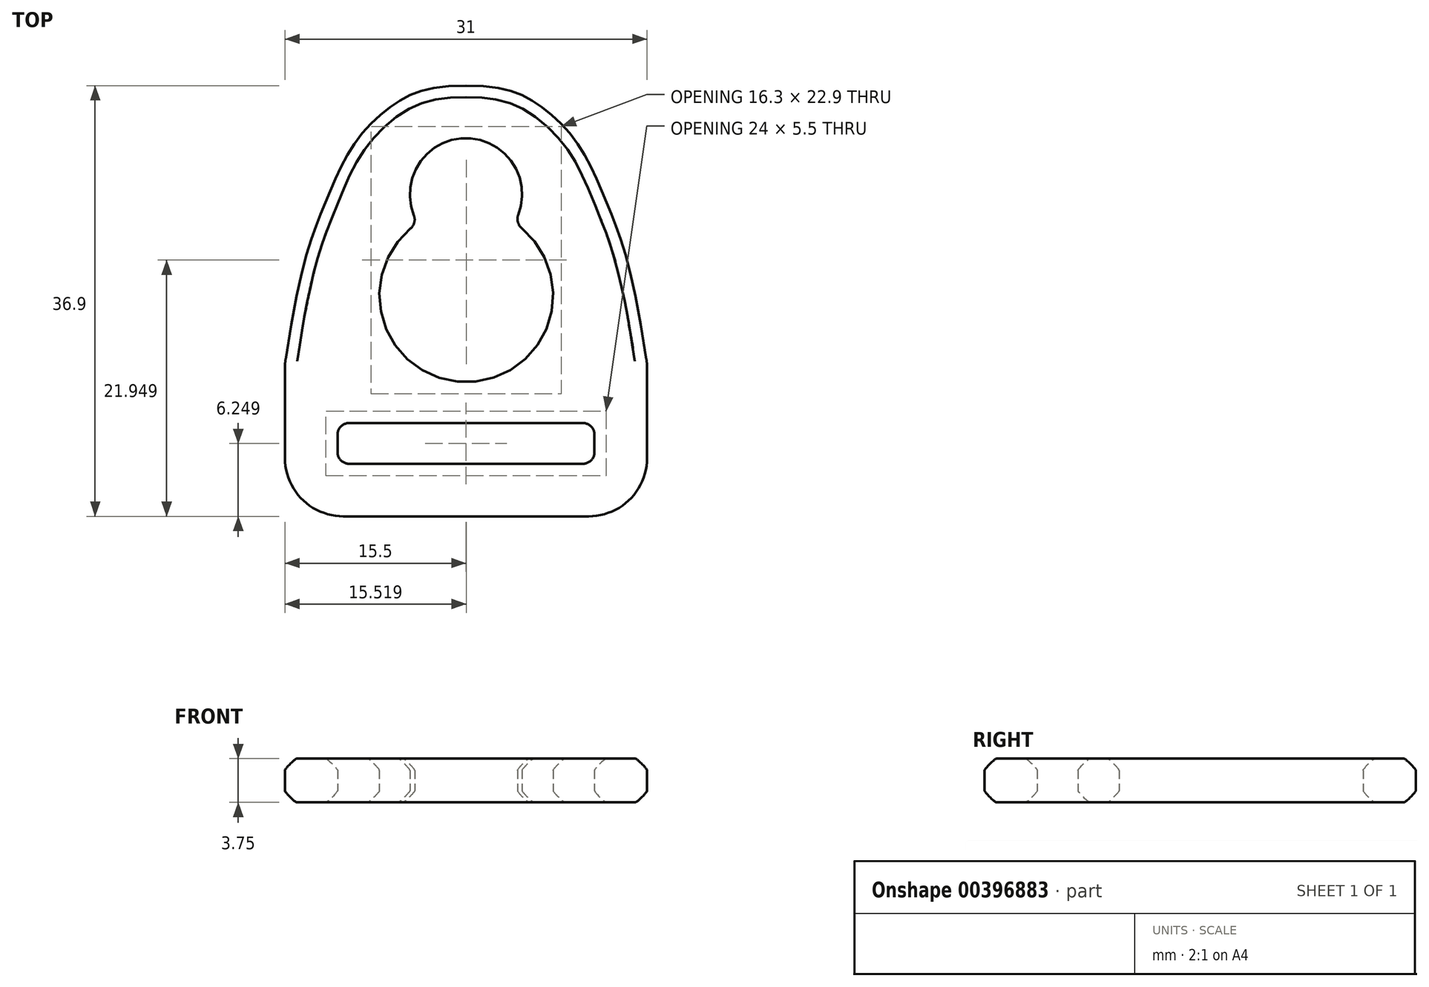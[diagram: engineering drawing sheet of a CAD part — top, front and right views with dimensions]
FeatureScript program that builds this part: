
annotation { "Feature Type Name" : "Feature", "Feature Type Description" : "" }
export const myFeature = defineFeature(function(context is Context, id is Id, definition is map)
    precondition{}
    {
        {
            var Q0;
            Q0=qCreatedBy(makeId("Top.planeOp"),FACE);
            var sketch = newSketch(context, id + "F0", { "sketchPlane" : qUnion([Q0])});
            skCircle(sketch, "E0", {"center": v(0.03, 5.86) * mm, "radius": 7.45 * mm});
            skCircle(sketch, "E1", {"center": v(0, 14.5) * mm, "radius": 4.8 * mm});
            skLineSegment(sketch, "E2", {"start": v(0, -1.58) * mm, "end": v(0, 19.32) * mm, "construction": true});
            skLineSegment(sketch, "E3.bottom", {"start": v(11, -8.58) * mm, "end": v(-11, -8.58) * mm});
            skLineSegment(sketch, "E3.top", {"start": v(11, -5.08) * mm, "end": v(-11, -5.08) * mm});
            skLineSegment(sketch, "E3.left", {"start": v(11, -8.58) * mm, "end": v(11, -5.08) * mm});
            skLineSegment(sketch, "E3.right", {"start": v(-11, -8.58) * mm, "end": v(-11, -5.08) * mm});
            skPoint(sketch, "E3.middle", {"position": v(0, -6.83) * mm});
            skLineSegment(sketch, "E4", {"start": v(0, -1.58) * mm, "end": v(0, -5.08) * mm, "construction": true});
            skPoint(sketch, "E4.endSnap0", {"position": v(0, -5.08) * mm});
            skLineSegment(sketch, "E5", {"start": v(-11, -8.58) * mm, "end": v(-15.5, -8.58) * mm, "construction": true});
            skLineSegment(sketch, "E6", {"start": v(-15.5, -8.58) * mm, "end": v(-15.5, -13.08) * mm, "construction": true});
            skLineSegment(sketch, "E7", {"start": v(11, -6.83) * mm, "end": v(15.5, -6.83) * mm, "construction": true});
            skLineSegment(sketch, "E8", {"start": v(0, 19.32) * mm, "end": v(0, 23.82) * mm, "construction": true});
            skLineSegment(sketch, "E9.bottom", {"start": v(-15.5, -13.08) * mm, "end": v(15.5, -13.08) * mm});
            skLineSegment(sketch, "E9.top", {"start": v(-15.5, 23.82) * mm, "end": v(15.5, 23.82) * mm});
            skLineSegment(sketch, "E9.left", {"start": v(-15.5, -13.08) * mm, "end": v(-15.5, 23.82) * mm});
            skLineSegment(sketch, "E9.right", {"start": v(15.5, -13.08) * mm, "end": v(15.5, 23.82) * mm});
            skFitSpline(sketch, "E10", {"points": [v(-15.5, 0) * mm, v(-12.1, 13.64) * mm, v(-9.63, 18.74) * mm, v(-5.82, 22.43) * mm, v(0, 23.82) * mm], "startDerivative": vector(11.5, 77.14) * mm, "endDerivative": vector(37.83, 0) * mm});
            skFitSpline(sketch, "E11.MirrorCS", {"points": [v(15.5, 0) * mm, v(12.1, 13.64) * mm, v(9.63, 18.74) * mm, v(5.82, 22.43) * mm, v(0, 23.82) * mm], "startDerivative": vector(-11.5, 77.14) * mm, "endDerivative": vector(-37.83, 0) * mm});
            skLineSegment(sketch, "E12", {"start": v(-4.13, 12.04) * mm, "end": v(4.13, 12.04) * mm, "construction": true});
            skSolve(sketch);
        }
        {
            var Q0;
            Q0=makeQuery(id+"F0.imprint","IMPRINT",FACE,{"disambiguationData":[TD([[makeQuery(id+"F0.imprint","IMPRINT",EDGE,{"derivedFrom":sQuery(id+"F0.wireOp",EDGE,"E3.bottom")}),1.0]])]});
            extrude(context, id + "F1", {"entities" : qUnion([Q0]), "depth" : 3.75 * mm});
        }
        {
            var Q0;
            Q0=makeQuery(id+"F1.opExtrude","SWEPT_EDGE",EDGE,{"disambiguationData":[OSD([sQuery(id+"F0.wireOp",EDGE,"E9.left"),sQuery(id+"F0.wireOp",EDGE,"E10")])]});
            var Q1;
            Q1=makeQuery(id+"F1.opExtrude","SWEPT_EDGE",EDGE,{"disambiguationData":[OSD([sQuery(id+"F0.wireOp",EDGE,"E9.bottom"),sQuery(id+"F0.wireOp",EDGE,"E9.left")])]});
            var Q2;
            Q2=makeQuery(id+"F1.opExtrude","SWEPT_EDGE",EDGE,{"disambiguationData":[OSD([sQuery(id+"F0.wireOp",EDGE,"E9.right"),sQuery(id+"F0.wireOp",EDGE,"E11.MirrorCS")])]});
            var Q3;
            Q3=makeQuery(id+"F1.opExtrude","SWEPT_EDGE",EDGE,{"disambiguationData":[OSD([sQuery(id+"F0.wireOp",EDGE,"E9.bottom"),sQuery(id+"F0.wireOp",EDGE,"E9.right")])]});
            fillet(context, id + "F2", {"entities" : qUnion([Q0, Q1, Q2, Q3]), "radius" : 5 * mm, "tangentPropagation" : true, "allowEdgeOverflow" : false});
        }
        {
            var Q0;
            Q0=makeQuery(id+"F1.opExtrude","SWEPT_EDGE",EDGE,{"disambiguationData":[OSD([sQuery(id+"F0.wireOp",EDGE,"E3.top"),sQuery(id+"F0.wireOp",EDGE,"E3.right")])]});
            var Q1;
            Q1=makeQuery(id+"F1.opExtrude","SWEPT_EDGE",EDGE,{"disambiguationData":[OSD([sQuery(id+"F0.wireOp",EDGE,"E3.bottom"),sQuery(id+"F0.wireOp",EDGE,"E3.right")])]});
            var Q2;
            Q2=makeQuery(id+"F1.opExtrude","SWEPT_EDGE",EDGE,{"disambiguationData":[OSD([sQuery(id+"F0.wireOp",EDGE,"E3.top"),sQuery(id+"F0.wireOp",EDGE,"E3.left")])]});
            var Q3;
            Q3=makeQuery(id+"F1.opExtrude","SWEPT_EDGE",EDGE,{"disambiguationData":[OSD([sQuery(id+"F0.wireOp",EDGE,"E3.bottom"),sQuery(id+"F0.wireOp",EDGE,"E3.left")])]});
            var Q4;
            {var subQ0=sQuery(id+"F0.wireOp",EDGE,"E1");var subQ1=sQuery(id+"F0.wireOp",EDGE,"E0");Q4=makeQuery(id+"F1.opExtrude","SWEPT_EDGE",EDGE,{"disambiguationData":[OSD([subQ1,subQ0]),TDD([makeQuery(id+"F0.imprint","INTERSECT",VERTEX,{"disambiguationData":[OD(0.0)],"derivedFrom":[subQ1,subQ0]})])]});}
            var Q5;
            {var subQ0=sQuery(id+"F0.wireOp",EDGE,"E1");var subQ1=sQuery(id+"F0.wireOp",EDGE,"E0");Q5=makeQuery(id+"F1.opExtrude","SWEPT_EDGE",EDGE,{"disambiguationData":[OSD([subQ1,subQ0]),TDD([makeQuery(id+"F0.imprint","INTERSECT",VERTEX,{"disambiguationData":[OD(1.0)],"derivedFrom":[subQ1,subQ0]})])]});}
            fillet(context, id + "F3", {"entities" : qUnion([Q0, Q1, Q2, Q3, Q4, Q5]), "radius" : 1 * mm, "tangentPropagation" : true, "allowEdgeOverflow" : false});
        }
        {
            var Q0;
            Q0=makeQuery(id+"F1.opExtrude","CAP_EDGE",EDGE,{"disambiguationData":[OSD([sQuery(id+"F0.wireOp",EDGE,"E3.top")])],"isStart":false});
            var Q1;
            Q1=makeQuery(id+"F1.opExtrude","CAP_EDGE",EDGE,{"disambiguationData":[OSD([sQuery(id+"F0.wireOp",EDGE,"E3.top")])],"isStart":true});
            var Q2;
            Q2=makeQuery(id+"F1.opExtrude","CAP_EDGE",EDGE,{"disambiguationData":[OSD([sQuery(id+"F0.wireOp",EDGE,"E0")])],"isStart":false});
            var Q3;
            Q3=makeQuery(id+"F1.opExtrude","CAP_EDGE",EDGE,{"disambiguationData":[OSD([sQuery(id+"F0.wireOp",EDGE,"E0")])],"isStart":true});
            var Q4;
            Q4=makeQuery(id+"F1.opExtrude","CAP_EDGE",EDGE,{"disambiguationData":[OSD([sQuery(id+"F0.wireOp",EDGE,"E1")])],"isStart":false});
            var Q5;
            Q5=makeQuery(id+"F1.opExtrude","CAP_EDGE",EDGE,{"disambiguationData":[OSD([sQuery(id+"F0.wireOp",EDGE,"E1")])],"isStart":true});
            var Q6;
            Q6=makeQuery(id+"F1.opExtrude","CAP_EDGE",EDGE,{"disambiguationData":[OSD([sQuery(id+"F0.wireOp",EDGE,"E11.MirrorCS")])],"isStart":false});
            var Q7;
            Q7=makeQuery(id+"F1.opExtrude","CAP_EDGE",EDGE,{"disambiguationData":[OSD([sQuery(id+"F0.wireOp",EDGE,"E10")])],"isStart":false});
            var Q8;
            Q8=makeQuery(id+"F1.opExtrude","CAP_EDGE",EDGE,{"disambiguationData":[OSD([sQuery(id+"F0.wireOp",EDGE,"E10")])],"isStart":true});
            var Q9;
            Q9=makeQuery(id+"F1.opExtrude","CAP_EDGE",EDGE,{"disambiguationData":[OSD([sQuery(id+"F0.wireOp",EDGE,"E9.left")])],"isStart":true});
            var Q10;
            Q10=makeQuery(id+"F1.opExtrude","CAP_EDGE",EDGE,{"disambiguationData":[OSD([sQuery(id+"F0.wireOp",EDGE,"E9.left")])],"isStart":false});
            var Q11;
            Q11=makeQuery(id+"F1.opExtrude","SWEPT_FACE",FACE,{"disambiguationData":[OSD([sQuery(id+"F0.wireOp",EDGE,"E11.MirrorCS")])]});
            var Q12;
            {var subQ0=sQuery(id+"F0.wireOp",EDGE,"E9.right");var subQ1=sQuery(id+"F0.wireOp",EDGE,"E9.bottom");Q12=makeQuery(id+"F2.opFillet","BLEND_EDGE",EDGE,{"blendedFrom":[makeQuery(id+"F1.opExtrude","SWEPT_EDGE",EDGE,{"disambiguationData":[OSD([subQ1,subQ0])]}),makeQuery(id+"F1.opExtrude","CAP_FACE",FACE,{"disambiguationData":[OSD([sQuery(id+"F0.wireOp",EDGE,"E0"),sQuery(id+"F0.wireOp",EDGE,"E1"),sQuery(id+"F0.wireOp",EDGE,"E3.bottom"),sQuery(id+"F0.wireOp",EDGE,"E3.top"),sQuery(id+"F0.wireOp",EDGE,"E3.left"),sQuery(id+"F0.wireOp",EDGE,"E3.right"),subQ1,sQuery(id+"F0.wireOp",EDGE,"E9.left"),subQ0,sQuery(id+"F0.wireOp",EDGE,"E10"),sQuery(id+"F0.wireOp",EDGE,"E11.MirrorCS")])],"isStart":true})],"blendedInto":[makeQuery(id+"F1.opExtrude","CAP_FACE",FACE,{"disambiguationData":[OSD([sQuery(id+"F0.wireOp",EDGE,"E0"),sQuery(id+"F0.wireOp",EDGE,"E1"),sQuery(id+"F0.wireOp",EDGE,"E3.bottom"),sQuery(id+"F0.wireOp",EDGE,"E3.top"),sQuery(id+"F0.wireOp",EDGE,"E3.left"),sQuery(id+"F0.wireOp",EDGE,"E3.right"),subQ1,sQuery(id+"F0.wireOp",EDGE,"E9.left"),subQ0,sQuery(id+"F0.wireOp",EDGE,"E10"),sQuery(id+"F0.wireOp",EDGE,"E11.MirrorCS")])],"isStart":true})]});}
            fillet(context, id + "F4", {"entities" : qUnion([Q0, Q1, Q2, Q3, Q4, Q5, Q6, Q7, Q8, Q9, Q10, Q11, Q12]), "radius" : 1 * mm, "tangentPropagation" : true, "rho" : .1, "crossSection" : FilletCrossSection.CONIC, "allowEdgeOverflow" : false});
        }
    });
